# Revit family: 79226
name_source: partatom
category: Aparatos sanitarios
revit_build: Autodesk Revit 2017 (Build: 20160225_1515(x64)
units: mm (PartAtom-declared; Revit-internal decimal feet)

## family parameters
Anfitrión = Cara
Compartido = No
Corte con vacíos al cargar = No
Cota de conector redondo = Diámetro de uso
Número OmniClass = 23.45.55.14
Punto de cálculo de habitación = No
Tipo de pieza = Normal
Título OmniClass = Single Faucets

## types (1)
- 79226
    Accionamiento = Manual
    CAUDAL = 6 l/min.
    CIERRE = Automático en 120 seg.
    Comentarios de tipo = Ahorro de agua y energia. Componentes integrados. Conexiones internas estancas. Suministrador con caja para empotrar. Cierre automático de electroválvula en caso de fallo de alimentación eléctrica. Aireador "Flowing Ecosystems". Aclarado automático c/24h. Pack de pila CR-P2 estanco. Temperatura máxima 70ºC
    Conexión AC = No
    Conexión AF = Sí
    Código de montaje = C1030220
    Descripción = Grifo eléctronico para lavabo de un agua para instalación mural.
    ENTRADA = Macho 1/2"
    Elevación por defecto = 1219 mm
    Fabricante = PRESTO IBÉRICA
    Imagen de tipo = <Ninguno>
    Material = LATON CROMADO
    Modelo = PRESTO DOMO SENSIA - P con Alimentador 12V 2 Inox
    PESO BRUTO = 1,500 Kg
    Presión Máxima = Max. 8 bar
    REFERENCIA = 79226
    TIPO DE AGUA = Fria
    Teléfono = (+34) 915 782 575
    URL = http://www.griferiasgalindo.com
